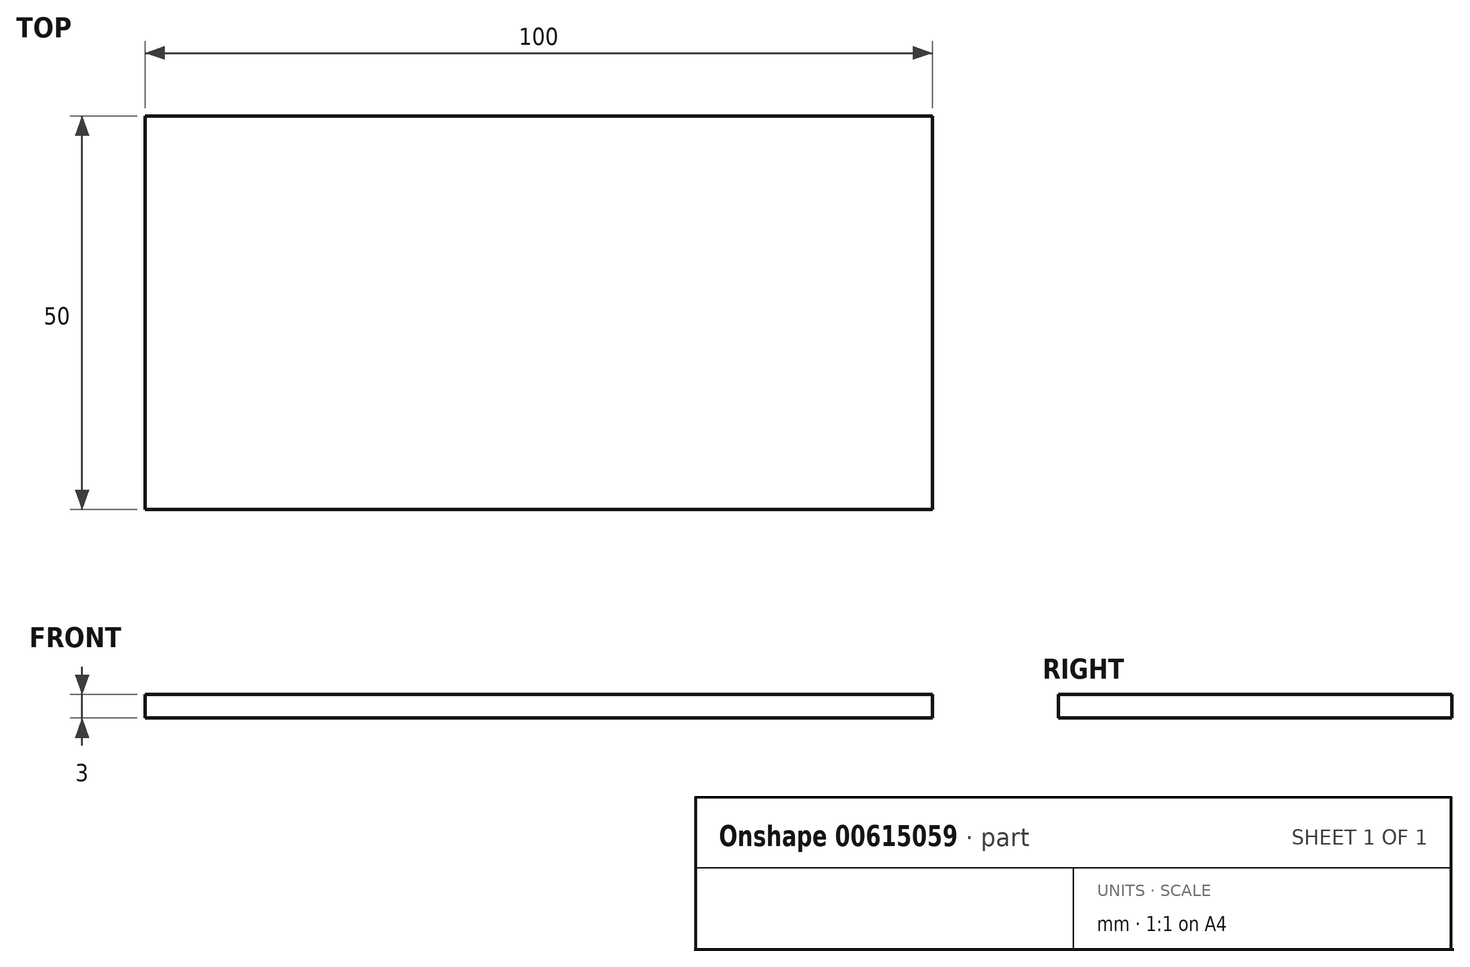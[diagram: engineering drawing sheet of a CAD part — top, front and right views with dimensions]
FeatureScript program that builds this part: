
annotation { "Feature Type Name" : "Feature", "Feature Type Description" : "" }
export const myFeature = defineFeature(function(context is Context, id is Id, definition is map)
    precondition{}
    {
        {
            var Q0;
            Q0=qCreatedBy(makeId("Top.planeOp"),FACE);
            var sketch = newSketch(context, id + "F0", { "sketchPlane" : qUnion([Q0])});
            skLineSegment(sketch, "E0.bottom", {"start": v(0, 0) * mm, "end": v(100, 0) * mm});
            skLineSegment(sketch, "E0.top", {"start": v(0, -50) * mm, "end": v(100, -50) * mm});
            skLineSegment(sketch, "E0.left", {"start": v(0, 0) * mm, "end": v(0, -50) * mm});
            skLineSegment(sketch, "E0.right", {"start": v(100, 0) * mm, "end": v(100, -50) * mm});
            skSolve(sketch);
        }
        {
            var Q0;
            Q0 = qSketchRegion(id + "F0", true);
            extrude(context, id + "F1", {"entities" : qUnion([Q0]), "depth" : 3 * mm, "offsetDistance" : 25 * mm});
        }
    });
